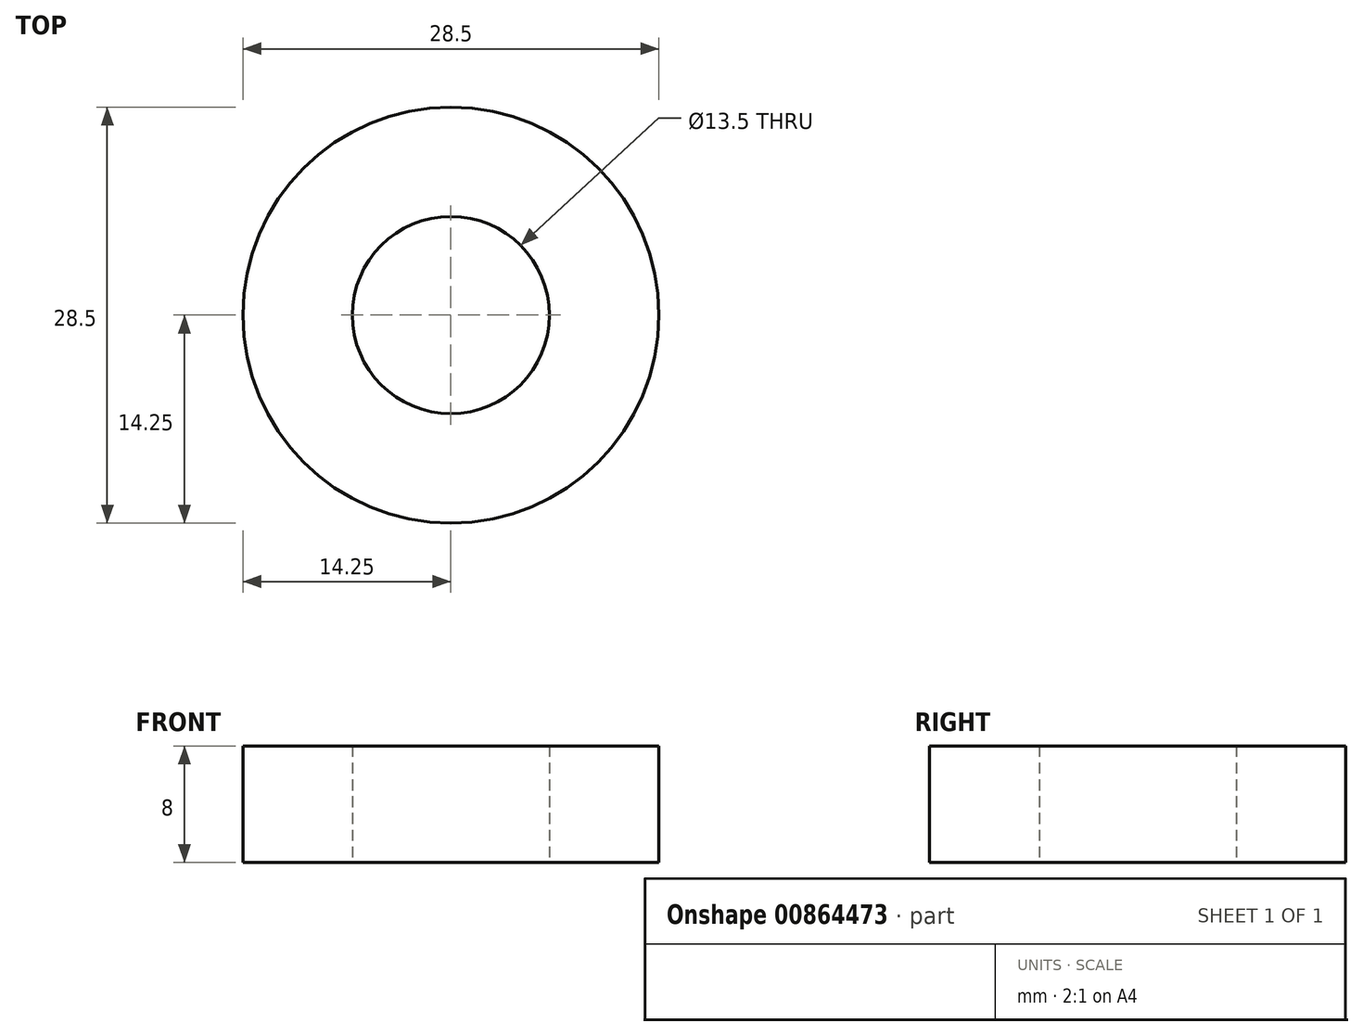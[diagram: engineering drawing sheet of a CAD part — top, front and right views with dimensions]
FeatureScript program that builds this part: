
annotation { "Feature Type Name" : "Feature", "Feature Type Description" : "" }
export const myFeature = defineFeature(function(context is Context, id is Id, definition is map)
    precondition{}
    {
        {
            var Q0;
            Q0=qCreatedBy(makeId("Top.planeOp"),FACE);
            var sketch = newSketch(context, id + "F0", { "sketchPlane" : qUnion([Q0])});
            skCircle(sketch, "E0", {"center": v(0, 0) * mm, "radius": 14.25 * mm});
            skCircle(sketch, "E1", {"center": v(0, 0) * mm, "radius": 6.75 * mm});
            skSolve(sketch);
        }
        {
            var Q0;
            Q0=makeQuery(id+"F0.imprint","IMPRINT",FACE,{"disambiguationData":[TD([[makeQuery(id+"F0.imprint","IMPRINT",EDGE,{"derivedFrom":sQuery(id+"F0.wireOp",EDGE,"E0")}),1.0]])]});
            extrude(context, id + "F1", {"entities" : qUnion([Q0]), "depth" : 8 * mm, "offsetDistance" : 25 * mm});
        }
    });
